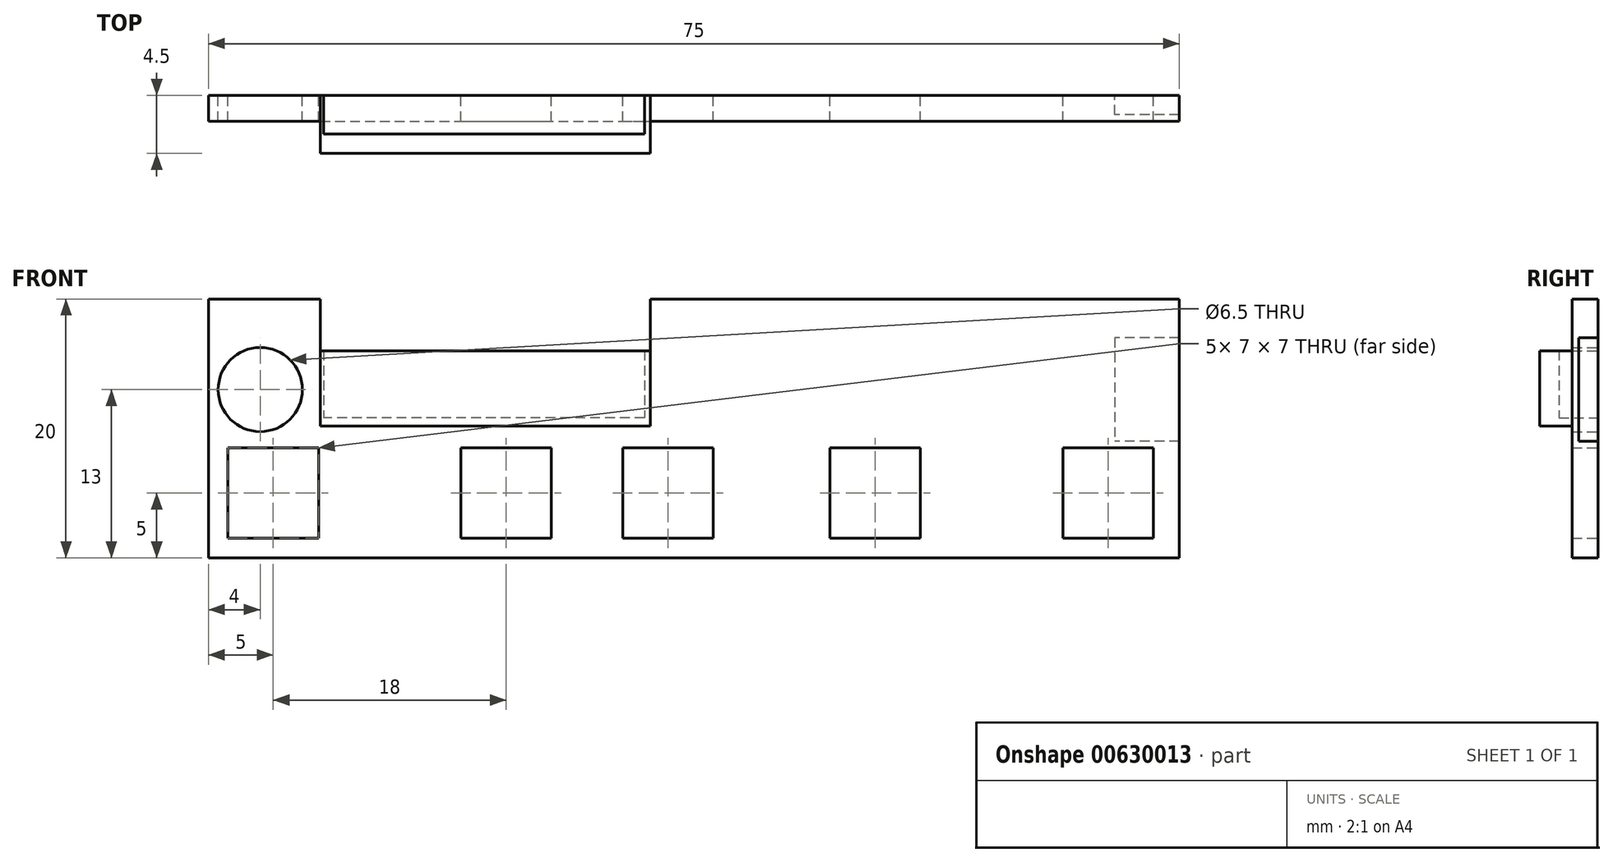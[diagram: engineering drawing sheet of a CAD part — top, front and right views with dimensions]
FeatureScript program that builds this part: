
annotation { "Feature Type Name" : "Feature", "Feature Type Description" : "" }
export const myFeature = defineFeature(function(context is Context, id is Id, definition is map)
    precondition{}
    {
        {
            var Q0;
            Q0=qCreatedBy(makeId("Front.planeOp"),FACE);
            var sketch = newSketch(context, id + "F0", { "sketchPlane" : qUnion([Q0])});
            skPoint(sketch, "E0.middle", {"position": v(0, 0) * mm});
            skLineSegment(sketch, "E1.bottom", {"start": v(-37.5, -8) * mm, "end": v(37.5, -8) * mm});
            skLineSegment(sketch, "E1.top", {"start": v(-37.5, 8) * mm, "end": v(37.5, 8) * mm});
            skLineSegment(sketch, "E1.left", {"start": v(-37.5, -8) * mm, "end": v(-37.5, 8) * mm});
            skLineSegment(sketch, "E1.right", {"start": v(37.5, -8) * mm, "end": v(37.5, 8) * mm});
            skLineSegment(sketch, "E2.top", {"start": v(-37.5, 12) * mm, "end": v(37.5, 12) * mm});
            skLineSegment(sketch, "E2.left", {"start": v(-37.5, -8) * mm, "end": v(-37.5, 12) * mm});
            skLineSegment(sketch, "E2.right", {"start": v(37.5, -8) * mm, "end": v(37.5, 12) * mm});
            skLineSegment(sketch, "E3.bottom", {"start": v(-36, -6.5) * mm, "end": v(-29, -6.5) * mm});
            skLineSegment(sketch, "E3.top", {"start": v(-36, 0.5) * mm, "end": v(-29, 0.5) * mm});
            skLineSegment(sketch, "E3.left", {"start": v(-36, -6.5) * mm, "end": v(-36, 0.5) * mm});
            skLineSegment(sketch, "E3.right", {"start": v(-29, -6.5) * mm, "end": v(-29, 0.5) * mm});
            skPoint(sketch, "E3.middle", {"position": v(-32.5, -3) * mm});
            skLineSegment(sketch, "E4.bottom", {"start": v(-18, -6.5) * mm, "end": v(-11, -6.5) * mm});
            skLineSegment(sketch, "E4.top", {"start": v(-18, 0.5) * mm, "end": v(-11, 0.5) * mm});
            skLineSegment(sketch, "E4.left", {"start": v(-18, -6.5) * mm, "end": v(-18, 0.5) * mm});
            skLineSegment(sketch, "E4.right", {"start": v(-11, -6.5) * mm, "end": v(-11, 0.5) * mm});
            skPoint(sketch, "E4.middle", {"position": v(-14.5, -3) * mm});
            skLineSegment(sketch, "E5.bottom", {"start": v(-5.5, -6.5) * mm, "end": v(1.5, -6.5) * mm});
            skLineSegment(sketch, "E5.top", {"start": v(-5.5, 0.5) * mm, "end": v(1.5, 0.5) * mm});
            skLineSegment(sketch, "E5.left", {"start": v(-5.5, -6.5) * mm, "end": v(-5.5, 0.5) * mm});
            skLineSegment(sketch, "E5.right", {"start": v(1.5, -6.5) * mm, "end": v(1.5, 0.5) * mm});
            skPoint(sketch, "E5.middle", {"position": v(-2, -3) * mm});
            skLineSegment(sketch, "E6.bottom", {"start": v(10.5, -6.5) * mm, "end": v(17.5, -6.5) * mm});
            skLineSegment(sketch, "E6.top", {"start": v(10.5, 0.5) * mm, "end": v(17.5, 0.5) * mm});
            skLineSegment(sketch, "E6.left", {"start": v(10.5, -6.5) * mm, "end": v(10.5, 0.5) * mm});
            skLineSegment(sketch, "E6.right", {"start": v(17.5, -6.5) * mm, "end": v(17.5, 0.5) * mm});
            skPoint(sketch, "E6.middle", {"position": v(14, -3) * mm});
            skLineSegment(sketch, "E7.bottom", {"start": v(28.5, -6.5) * mm, "end": v(35.5, -6.5) * mm});
            skLineSegment(sketch, "E7.top", {"start": v(28.5, 0.5) * mm, "end": v(35.5, 0.5) * mm});
            skLineSegment(sketch, "E7.left", {"start": v(28.5, -6.5) * mm, "end": v(28.5, 0.5) * mm});
            skLineSegment(sketch, "E7.right", {"start": v(35.5, -6.5) * mm, "end": v(35.5, 0.5) * mm});
            skPoint(sketch, "E7.middle", {"position": v(32, -3) * mm});
            skCircle(sketch, "E8", {"center": v(-33.5, 5) * mm, "radius": 3.25 * mm});
            skLineSegment(sketch, "E9.bottom", {"start": v(-28.85, 12) * mm, "end": v(-3.35, 12) * mm});
            skLineSegment(sketch, "E9.top", {"start": v(-28.85, 2.19) * mm, "end": v(-3.35, 2.19) * mm});
            skLineSegment(sketch, "E9.left", {"start": v(-28.85, 12) * mm, "end": v(-28.85, 2.19) * mm});
            skLineSegment(sketch, "E9.right", {"start": v(-3.35, 12) * mm, "end": v(-3.35, 2.19) * mm});
            skSolve(sketch);
        }
        {
            var Q0;
            {var subQ0=sQuery(id+"F0.wireOp",EDGE,"E2.right");var subQ1=sQuery(id+"F0.wireOp",EDGE,"E1.top");var subQ2=makeQuery(id+"F0.imprint","INTERSECT",VERTEX,{"derivedFrom":[subQ1,subQ0]});Q0=makeQuery(id+"F0.imprint","IMPRINT",FACE,{"disambiguationData":[TD([[makeQuery(id+"F0.imprint","IMPRINT",EDGE,{"disambiguationData":[TD([[subQ2,1.0]])],"derivedFrom":subQ1}),1.0]])]});}
            var Q1;
            {var subQ0=sQuery(id+"F0.wireOp",EDGE,"E2.left");var subQ1=sQuery(id+"F0.wireOp",EDGE,"E1.top");var subQ2=makeQuery(id+"F0.imprint","INTERSECT",VERTEX,{"derivedFrom":[subQ1,subQ0]});Q1=makeQuery(id+"F0.imprint","IMPRINT",FACE,{"disambiguationData":[TD([[makeQuery(id+"F0.imprint","IMPRINT",EDGE,{"disambiguationData":[TD([[subQ2,-1.0]])],"derivedFrom":subQ1}),1.0]])]});}
            var Q2;
            {var subQ9=sQuery(id+"F0.wireOp",EDGE,"E1.bottom");Q2=makeQuery(id+"F0.imprint","IMPRINT",FACE,{"disambiguationData":[TD([[makeQuery(id+"F0.imprint","IMPRINT",EDGE,{"derivedFrom":subQ9}),1.0]])]});}
            extrude(context, id + "F1", {"entities" : qUnion([Q0, Q1, Q2]), "flatOperationType" : FlatOperationType.REMOVE, "depth" : 2 * mm, "offsetDistance" : 25.4 * mm, "domain" : OperationDomain.MODEL});
        }
        {
            var Q0;
            {var subQ5=sQuery(id+"F0.wireOp",EDGE,"E9.bottom");Q0=makeQuery(id+"F0.imprint","IMPRINT",FACE,{"disambiguationData":[TD([[makeQuery(id+"F0.imprint","IMPRINT",EDGE,{"derivedFrom":subQ5}),-1.0]])]});}
            var Q1;
            {var subQ5=sQuery(id+"F0.wireOp",EDGE,"E9.top");Q1=makeQuery(id+"F0.imprint","IMPRINT",FACE,{"disambiguationData":[TD([[makeQuery(id+"F0.imprint","IMPRINT",EDGE,{"derivedFrom":subQ5}),1.0]])]});}
            extrude(context, id + "F2", {"entities" : qUnion([Q0, Q1]), "operationType" : NewBodyOperationType.ADD, "flatOperationType" : FlatOperationType.REMOVE, "depth" : 4.5 * mm, "offsetDistance" : 25.4 * mm, "domain" : OperationDomain.MODEL});
        }
        {
            var Q0;
            {var subQ0=sQuery(id+"F0.wireOp",EDGE,"E9.right");var subQ1=sQuery(id+"F0.wireOp",EDGE,"E9.left");var subQ2=sQuery(id+"F0.wireOp",EDGE,"E9.top");Q0=makeQuery(id+"F2.boolean.opBoolean","MERGE",FACE,{"derivedFrom":[makeQuery(id+"F1.opExtrude","CAP_FACE",FACE,{"disambiguationData":[OSD([sQuery(id+"F0.wireOp",EDGE,"E1.bottom"),sQuery(id+"F0.wireOp",EDGE,"E2.top"),sQuery(id+"F0.wireOp",EDGE,"E2.left"),sQuery(id+"F0.wireOp",EDGE,"E2.right"),sQuery(id+"F0.wireOp",EDGE,"E3.bottom"),sQuery(id+"F0.wireOp",EDGE,"E3.top"),sQuery(id+"F0.wireOp",EDGE,"E3.left"),sQuery(id+"F0.wireOp",EDGE,"E3.right"),sQuery(id+"F0.wireOp",EDGE,"E4.bottom"),sQuery(id+"F0.wireOp",EDGE,"E4.top"),sQuery(id+"F0.wireOp",EDGE,"E4.left"),sQuery(id+"F0.wireOp",EDGE,"E4.right"),sQuery(id+"F0.wireOp",EDGE,"E5.bottom"),sQuery(id+"F0.wireOp",EDGE,"E5.top"),sQuery(id+"F0.wireOp",EDGE,"E5.left"),sQuery(id+"F0.wireOp",EDGE,"E5.right"),sQuery(id+"F0.wireOp",EDGE,"E6.bottom"),sQuery(id+"F0.wireOp",EDGE,"E6.top"),sQuery(id+"F0.wireOp",EDGE,"E6.left"),sQuery(id+"F0.wireOp",EDGE,"E6.right"),sQuery(id+"F0.wireOp",EDGE,"E7.bottom"),sQuery(id+"F0.wireOp",EDGE,"E7.top"),sQuery(id+"F0.wireOp",EDGE,"E7.left"),sQuery(id+"F0.wireOp",EDGE,"E7.right"),sQuery(id+"F0.wireOp",EDGE,"E8"),subQ2,subQ1,subQ0])],"isStart":true}),makeQuery(id+"F2.opExtrude","CAP_FACE",FACE,{"disambiguationData":[OSD([sQuery(id+"F0.wireOp",EDGE,"E9.bottom"),subQ2,subQ1,subQ0])],"isStart":true})]});}
            var sketch = newSketch(context, id + "F3", { "sketchPlane" : qUnion([Q0])});
            skLineSegment(sketch, "E10.bottom", {"start": v(3.81, 12) * mm, "end": v(28.6, 12) * mm});
            skLineSegment(sketch, "E10.top", {"start": v(3.81, 2.73) * mm, "end": v(28.6, 2.73) * mm});
            skLineSegment(sketch, "E10.left", {"start": v(3.81, 12) * mm, "end": v(3.81, 2.73) * mm});
            skLineSegment(sketch, "E10.right", {"start": v(28.6, 12) * mm, "end": v(28.6, 2.73) * mm});
            skSolve(sketch);
        }
        {
            var Q0;
            Q0=makeQuery(id+"F3.imprint","IMPRINT",FACE,{"disambiguationData":[TD([[makeQuery(id+"F3.imprint","IMPRINT",EDGE,{"derivedFrom":sQuery(id+"F3.wireOp",EDGE,"E10.top")}),-1.0]])]});
            var sketch = newSketch(context, id + "F4", { "sketchPlane" : qUnion([Q0])});
            skLineSegment(sketch, "E11.bottom", {"start": v(-37.5, 9) * mm, "end": v(-32.5, 9) * mm});
            skLineSegment(sketch, "E11.top", {"start": v(-37.5, 1) * mm, "end": v(-32.5, 1) * mm});
            skLineSegment(sketch, "E11.left", {"start": v(-37.5, 9) * mm, "end": v(-37.5, 1) * mm});
            skLineSegment(sketch, "E11.right", {"start": v(-32.5, 9) * mm, "end": v(-32.5, 1) * mm});
            skSolve(sketch);
        }
        {
            var Q0;
            Q0 = qSketchRegion(id + "F4", true);
            extrude(context, id + "F5", {"entities" : qUnion([Q0]), "operationType" : NewBodyOperationType.REMOVE, "oppositeDirection" : true, "depth" : 1.5 * mm, "offsetDistance" : 25.4 * mm});
        }
        {
            var Q0;
            Q0=makeQuery(id+"F3.imprint","IMPRINT",FACE,{"disambiguationData":[TD([[makeQuery(id+"F3.imprint","IMPRINT",EDGE,{"derivedFrom":sQuery(id+"F3.wireOp",EDGE,"E10.top")}),-1.0]])]});
            var sketch = newSketch(context, id + "F6", { "sketchPlane" : qUnion([Q0])});
            skLineSegment(sketch, "E12.bottom", {"start": v(3.8, 12.03) * mm, "end": v(28.6, 12.03) * mm});
            skLineSegment(sketch, "E12.top", {"start": v(3.8, 2.82) * mm, "end": v(28.6, 2.82) * mm});
            skLineSegment(sketch, "E12.left", {"start": v(3.8, 12.03) * mm, "end": v(3.8, 2.82) * mm});
            skLineSegment(sketch, "E12.right", {"start": v(28.6, 12.03) * mm, "end": v(28.6, 2.82) * mm});
            skSolve(sketch);
        }
        {
            var Q0;
            Q0 = qSketchRegion(id + "F6", true);
            extrude(context, id + "F7", {"entities" : qUnion([Q0]), "operationType" : NewBodyOperationType.REMOVE, "oppositeDirection" : true, "depth" : 3 * mm, "offsetDistance" : 25.4 * mm});
        }
    });
